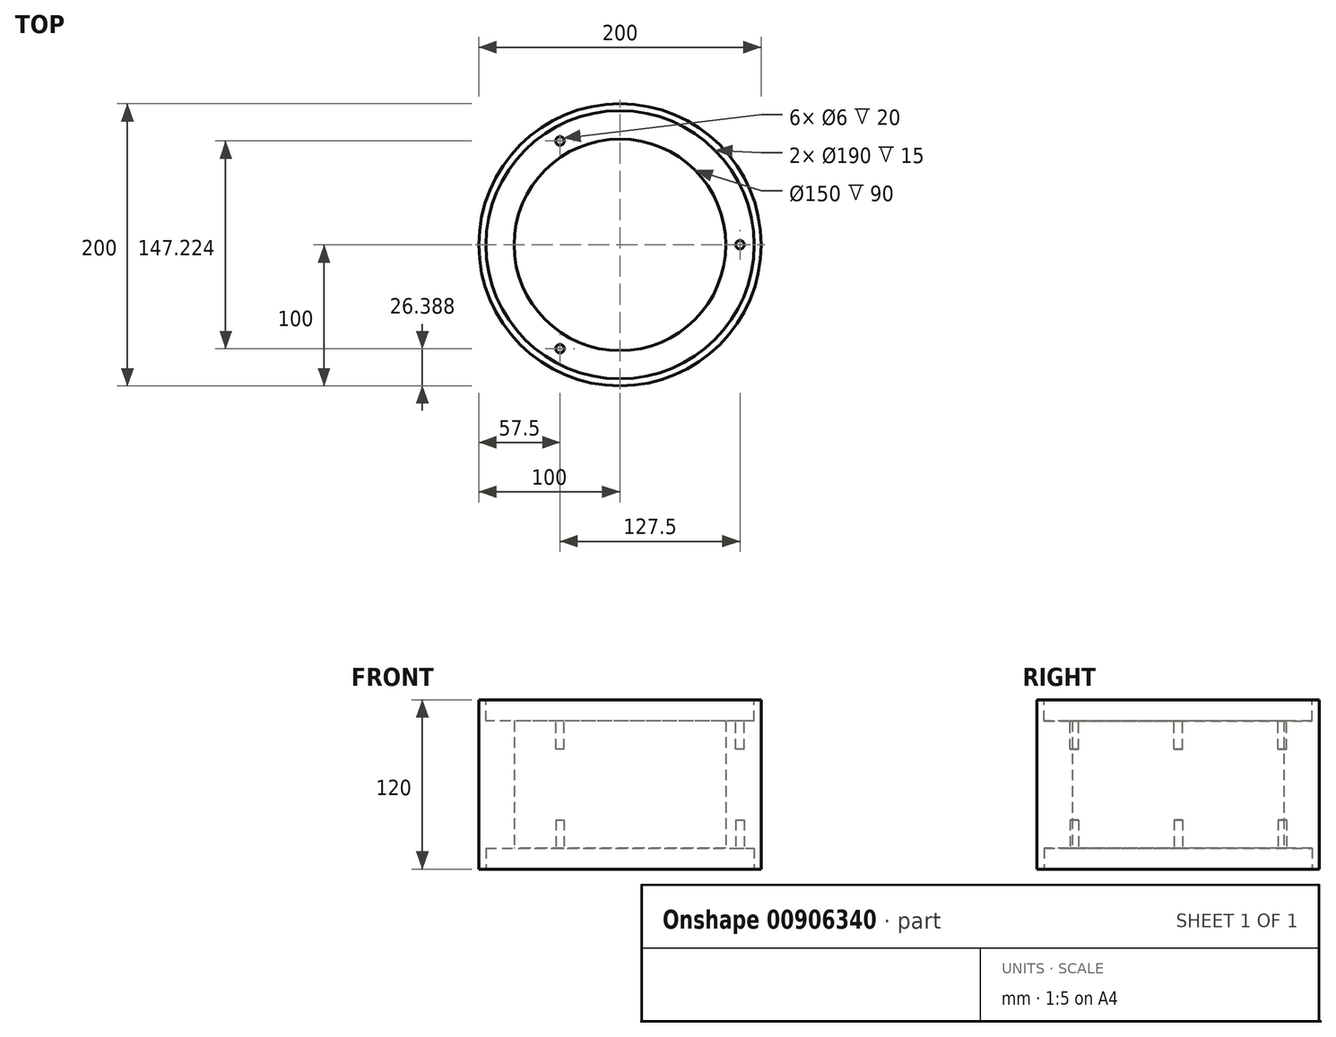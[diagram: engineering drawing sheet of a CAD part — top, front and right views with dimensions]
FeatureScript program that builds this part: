
annotation { "Feature Type Name" : "Feature", "Feature Type Description" : "" }
export const myFeature = defineFeature(function(context is Context, id is Id, definition is map)
    precondition{}
    {
        {
            var Q0;
            Q0=qCreatedBy(makeId("Top.planeOp"),FACE);
            var sketch = newSketch(context, id + "F0", { "sketchPlane" : qUnion([Q0])});
            skCircle(sketch, "E0", {"center": v(0, 0) * mm, "radius": 100 * mm});
            skCircle(sketch, "E1", {"center": v(0, 0) * mm, "radius": 75 * mm});
            skSolve(sketch);
        }
        {
            var Q0;
            Q0=makeQuery(id+"F0.imprint","IMPRINT",FACE,{"disambiguationData":[TD([[makeQuery(id+"F0.imprint","IMPRINT",EDGE,{"derivedFrom":sQuery(id+"F0.wireOp",EDGE,"E0")}),1.0]])]});
            extrude(context, id + "F1", {"entities" : qUnion([Q0]), "depth" : 120 * mm, "offsetDistance" : 25 * mm});
        }
        {
            var Q0;
            Q0=makeQuery(id+"F1.opExtrude","CAP_FACE",FACE,{"disambiguationData":[OSD([sQuery(id+"F0.wireOp",EDGE,"E0"),sQuery(id+"F0.wireOp",EDGE,"E1")])],"isStart":false});
            var sketch = newSketch(context, id + "F2", { "sketchPlane" : qUnion([Q0])});
            skCircle(sketch, "E2", {"center": v(0, 0) * mm, "radius": 95 * mm});
            skSolve(sketch);
        }
        {
            var Q0;
            Q0=makeQuery(id+"F2.imprint","IMPRINT",FACE,{"disambiguationData":[TD([[makeQuery(id+"F2.imprint","IMPRINT",EDGE,{"derivedFrom":sQuery(id+"F2.wireOp",EDGE,"E2")}),1.0]])]});
            extrude(context, id + "F3", {"entities" : qUnion([Q0]), "operationType" : NewBodyOperationType.REMOVE, "oppositeDirection" : true, "depth" : 15 * mm, "offsetDistance" : 25 * mm});
        }
        {
            var Q0;
            Q0=makeQuery(id+"F1.opExtrude","CAP_FACE",FACE,{"disambiguationData":[OSD([sQuery(id+"F0.wireOp",EDGE,"E0"),sQuery(id+"F0.wireOp",EDGE,"E1")])],"isStart":true});
            var sketch = newSketch(context, id + "F4", { "sketchPlane" : qUnion([Q0])});
            skCircle(sketch, "E3", {"center": v(0, 0) * mm, "radius": 95 * mm});
            skSolve(sketch);
        }
        {
            var Q0;
            Q0=makeQuery(id+"F4.imprint","IMPRINT",FACE,{"disambiguationData":[TD([[makeQuery(id+"F4.imprint","IMPRINT",EDGE,{"derivedFrom":sQuery(id+"F4.wireOp",EDGE,"E3")}),1.0]])]});
            extrude(context, id + "F5", {"entities" : qUnion([Q0]), "operationType" : NewBodyOperationType.REMOVE, "oppositeDirection" : true, "depth" : 15 * mm, "offsetDistance" : 25 * mm});
        }
        {
            var Q0;
            Q0=makeQuery(id+"F5.boolean.opBoolean","COPY",FACE,{"derivedFrom":makeQuery(id+"F5.opExtrude","CAP_FACE",FACE,{"disambiguationData":[OSD([sQuery(id+"F0.wireOp",EDGE,"E1"),sQuery(id+"F4.wireOp",EDGE,"E3")])],"isStart":false})});
            var sketch = newSketch(context, id + "F6", { "sketchPlane" : qUnion([Q0])});
            skLineSegment(sketch, "E4", {"start": v(0, 0) * mm, "end": v(155.95, 0) * mm, "construction": true});
            skLineSegment(sketch, "E5", {"start": v(0, 0) * mm, "end": v(-60.8, -105.3) * mm, "construction": true});
            skLineSegment(sketch, "E6", {"start": v(0, 0) * mm, "end": v(-66.64, 115.43) * mm, "construction": true});
            skCircle(sketch, "E7", {"center": v(0, 0) * mm, "radius": 85 * mm, "construction": true});
            skCircle(sketch, "E8", {"center": v(85, 0) * mm, "radius": 3 * mm});
            skCircle(sketch, "E9", {"center": v(-42.5, -73.61) * mm, "radius": 3 * mm});
            skCircle(sketch, "E10", {"center": v(-42.5, 73.61) * mm, "radius": 3 * mm});
            skSolve(sketch);
        }
        {
            var Q0;
            Q0 = qSketchRegion(id + "F6", true);
            extrude(context, id + "F7", {"entities" : qUnion([Q0]), "operationType" : NewBodyOperationType.REMOVE, "oppositeDirection" : true, "depth" : 20 * mm, "offsetDistance" : 25 * mm});
        }
        {
            var Q0;
            Q0=makeQuery(id+"F3.boolean.opBoolean","COPY",FACE,{"derivedFrom":makeQuery(id+"F3.opExtrude","CAP_FACE",FACE,{"disambiguationData":[OSD([sQuery(id+"F0.wireOp",EDGE,"E1"),sQuery(id+"F2.wireOp",EDGE,"E2")])],"isStart":false})});
            var sketch = newSketch(context, id + "F8", { "sketchPlane" : qUnion([Q0])});
            skLineSegment(sketch, "E11", {"start": v(0, 0) * mm, "end": v(131.3, 0) * mm, "construction": true});
            skLineSegment(sketch, "E12", {"start": v(0, 0) * mm, "end": v(-70.3, -121.78) * mm, "construction": true});
            skLineSegment(sketch, "E13", {"start": v(0, 0) * mm, "end": v(-77, 133.38) * mm, "construction": true});
            skCircle(sketch, "E14", {"center": v(0, 0) * mm, "radius": 85 * mm, "construction": true});
            skCircle(sketch, "E15", {"center": v(85, 0) * mm, "radius": 3 * mm});
            skCircle(sketch, "E16", {"center": v(-42.5, -73.61) * mm, "radius": 3 * mm});
            skCircle(sketch, "E17", {"center": v(-42.5, 73.61) * mm, "radius": 3 * mm});
            skSolve(sketch);
        }
        {
            var Q0;
            Q0 = qSketchRegion(id + "F8", true);
            var Q1;
            Q1 = qConstructionFilter(qBodyType(qCreatedBy(id + "F8" ,EDGE), BodyType.WIRE), ConstructionObject.NO);
            extrude(context, id + "F9", {"entities" : qUnion([Q0]), "operationType" : NewBodyOperationType.REMOVE, "surfaceEntities" : qUnion([Q1]), "oppositeDirection" : true, "depth" : 20 * mm, "offsetDistance" : 25 * mm});
        }
    });
